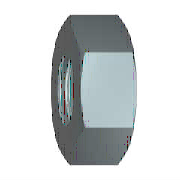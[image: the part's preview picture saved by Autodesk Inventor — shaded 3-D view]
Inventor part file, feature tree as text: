
AUTODESK INVENTOR PART (.ipt)
format: ipt  version: 2021 (Build 250183000, 183)  size: 163,840 bytes
history: native  units: mm (DEFAULTED — no unit token found)
features: sketch x3, chamfer x1, hole x1, other x1, plane x1
ambient origin geometry x7: Origin, YZ Plane, XZ Plane, X Axis, Y Axis, Z Axis, Center Point
bodies: Solid1 (feature_tree), Body (feature_tree)
feature tree (7):
  chamfer  "Chamfer1"  Angle=30.0deg  [1 undecoded]
  hole  "Thread"  [1 undecoded]
  other  "Work Axis1"
  plane  "Work Plane1"
  sketch  "Sketch1"  dims[d0=15.011107mm]
  sketch  "Sketch2"  dims[d1=6.8mm]
  sketch  "Sketch3"  dims[d2=0.0mm d3=30.0deg d4=30.0deg d5=11.6mm d6=11.6mm d7=90.0deg d25=6.647mm d26=6.0mm d27=4.0mm d28=2.0mm d29=14.3117mm d30=8.0mm d31=20.594885mm d8=0.676582mm d9=30.0deg d10=0.676582mm d11=30.0deg d13=0.0mm d14=0.0mm d39=0.0mm d40=0.676582mm d41=0.676582mm d42=0.0mm]
note: 2 required parameter values undecoded (feature->parameter linkage not recoverable at this tier; creation-order binding heuristic only, values carry confidence <= 0.55)
